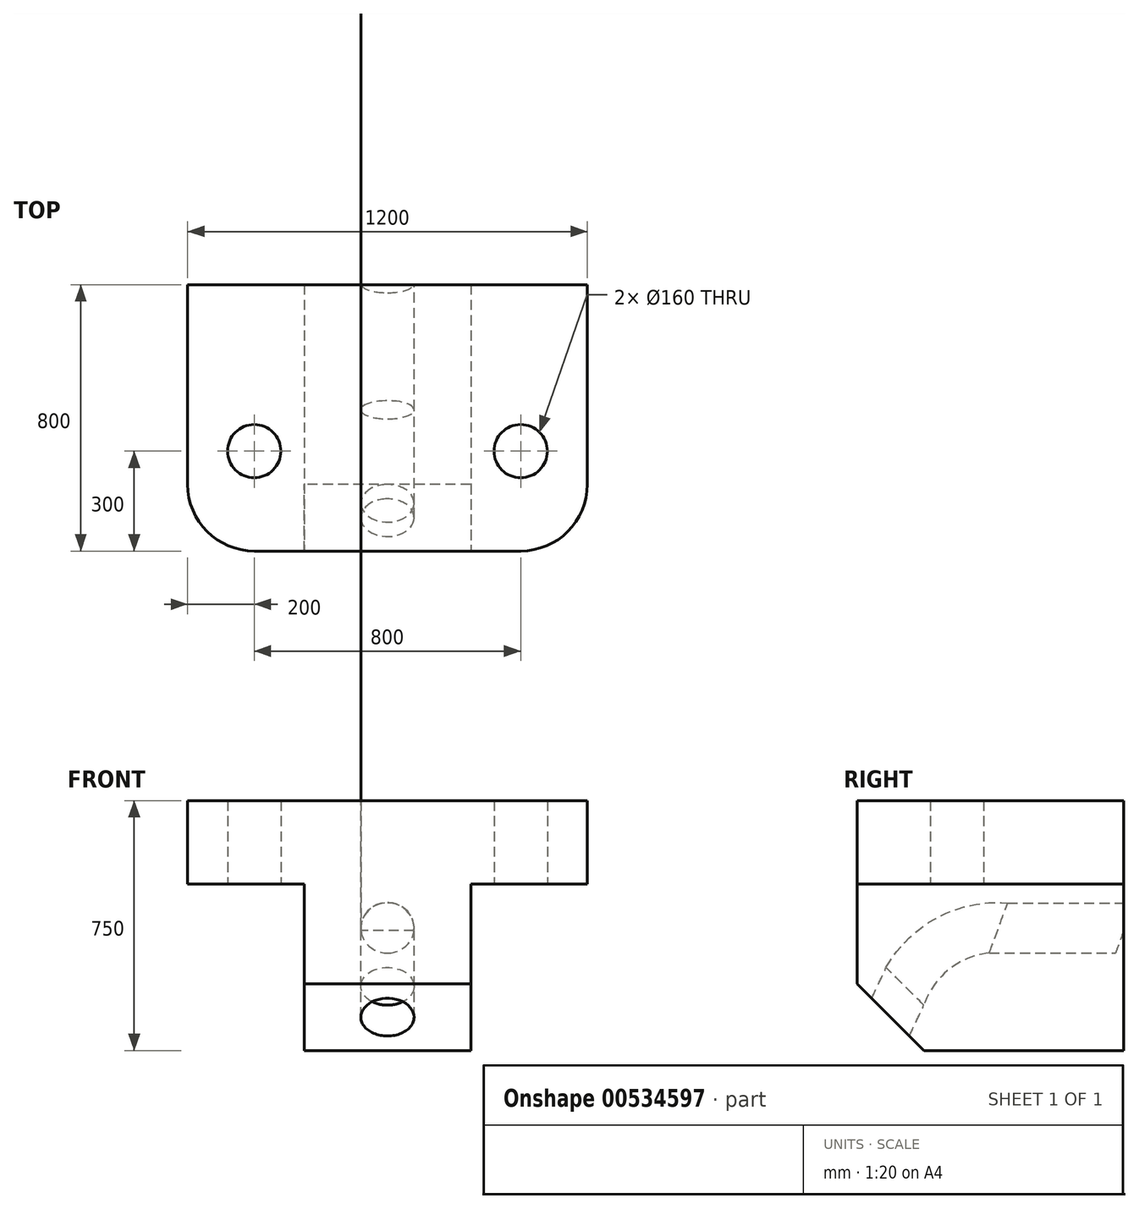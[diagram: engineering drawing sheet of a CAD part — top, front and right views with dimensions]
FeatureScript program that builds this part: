
annotation { "Feature Type Name" : "Feature", "Feature Type Description" : "" }
export const myFeature = defineFeature(function(context is Context, id is Id, definition is map)
    precondition{}
    {
        {
            var Q0;
            Q0=qCreatedBy(makeId("Top.planeOp"),FACE);
            var sketch = newSketch(context, id + "F0", { "sketchPlane" : qUnion([Q0])});
            skLineSegment(sketch, "E0.bottom", {"start": v(400, -400) * mm, "end": v(-400, -400) * mm});
            skLineSegment(sketch, "E0.top", {"start": v(600, 400) * mm, "end": v(-600, 400) * mm});
            skLineSegment(sketch, "E0.left", {"start": v(600, -200) * mm, "end": v(600, 400) * mm});
            skLineSegment(sketch, "E0.right", {"start": v(-600, -200) * mm, "end": v(-600, 400) * mm});
            skPoint(sketch, "E0.middle", {"position": v(0, 0) * mm});
            skPoint(sketch, "E1.visualSharp", {"position": v(-600, -400) * mm});
            skArc(sketch, "E1.filletArc", {"start": v(-600, -200) * mm, "mid": v(-541.42, -341.42) * mm, "end": v(-400, -400) * mm});
            skPoint(sketch, "E2.visualSharp", {"position": v(600, -400) * mm});
            skArc(sketch, "E2.filletArc", {"start": v(400, -400) * mm, "mid": v(541.42, -341.42) * mm, "end": v(600, -200) * mm});
            skSolve(sketch);
        }
        {
            var Q0;
            Q0 = qSketchRegion(id + "F0", true);
            extrude(context, id + "F1", {"entities" : qUnion([Q0]), "depth" : 250 * mm, "offsetDistance" : 25 * mm});
        }
        {
            var Q0;
            Q0=makeQuery(id+"F1.opExtrude","CAP_FACE",FACE,{"disambiguationData":[OSD([sQuery(id+"F0.wireOp",EDGE,"E0.bottom"),sQuery(id+"F0.wireOp",EDGE,"E0.top"),sQuery(id+"F0.wireOp",EDGE,"E0.left"),sQuery(id+"F0.wireOp",EDGE,"E0.right"),sQuery(id+"F0.wireOp",EDGE,"E1.filletArc"),sQuery(id+"F0.wireOp",EDGE,"E2.filletArc")])],"isStart":true});
            var sketch = newSketch(context, id + "F2", { "sketchPlane" : qUnion([Q0])});
            skCircle(sketch, "E3", {"center": v(-400, 100) * mm, "radius": 80 * mm});
            skCircle(sketch, "E4", {"center": v(400, 100) * mm, "radius": 80 * mm});
            skSolve(sketch);
        }
        {
            var Q0;
            Q0 = qSketchRegion(id + "F2", true);
            extrude(context, id + "F3", {"entities" : qUnion([Q0]), "operationType" : NewBodyOperationType.REMOVE, "oppositeDirection" : true, "depth" : 250 * mm, "offsetDistance" : 25 * mm});
        }
        {
            var Q0;
            Q0=makeQuery(id+"F1.opExtrude","CAP_FACE",FACE,{"disambiguationData":[OSD([sQuery(id+"F0.wireOp",EDGE,"E0.bottom"),sQuery(id+"F0.wireOp",EDGE,"E0.top"),sQuery(id+"F0.wireOp",EDGE,"E0.left"),sQuery(id+"F0.wireOp",EDGE,"E0.right"),sQuery(id+"F0.wireOp",EDGE,"E1.filletArc"),sQuery(id+"F0.wireOp",EDGE,"E2.filletArc")])],"isStart":true});
            var sketch = newSketch(context, id + "F4", { "sketchPlane" : qUnion([Q0])});
            skLineSegment(sketch, "E5.bottom", {"start": v(250, -400) * mm, "end": v(-250, -400) * mm});
            skLineSegment(sketch, "E5.top", {"start": v(250, 400) * mm, "end": v(-250, 400) * mm});
            skLineSegment(sketch, "E5.left", {"start": v(250, -400) * mm, "end": v(250, 400) * mm});
            skLineSegment(sketch, "E5.right", {"start": v(-250, -400) * mm, "end": v(-250, 400) * mm});
            skPoint(sketch, "E5.middle", {"position": v(0, 0) * mm});
            skSolve(sketch);
        }
        {
            var Q0;
            Q0 = qSketchRegion(id + "F4", true);
            extrude(context, id + "F5", {"entities" : qUnion([Q0]), "operationType" : NewBodyOperationType.ADD, "depth" : 500 * mm, "offsetDistance" : 25 * mm});
        }
        {
            var Q0;
            Q0=makeQuery(id+"F5.opExtrude","CAP_EDGE",EDGE,{"disambiguationData":[OSD([sQuery(id+"F4.wireOp",EDGE,"E5.top")])],"isStart":false});
            chamfer(context, id + "F6", {"entities" : qUnion([Q0]), "width" : 200 * mm, "tangentPropagation" : true});
        }
        {
            var Q0;
            Q0=makeQuery(id+"F6.opChamfer","BLEND_FACE",FACE,{"disambiguationData":[OSD([sQuery(id+"F4.wireOp",EDGE,"E5.top")])]});
            var sketch = newSketch(context, id + "F7", { "sketchPlane" : qUnion([Q0])});
            skCircle(sketch, "E6", {"center": v(0, -70.69) * mm, "radius": 80 * mm});
            skSolve(sketch);
        }
        {
            var Q0;
            Q0=makeQuery(id+"F5.opExtrude","SWEPT_FACE",FACE,{"disambiguationData":[OSD([sQuery(id+"F4.wireOp",EDGE,"E5.right")])]});
            var sketch = newSketch(context, id + "F8", { "sketchPlane" : qUnion([Q0])});
            skLineSegment(sketch, "E7", {"start": v(-21.12, -140) * mm, "end": v(-400, -140) * mm});
            skLineSegment(sketch, "E8", {"start": v(310.89, -442.19) * mm, "end": v(250.8, -313.26) * mm});
            skPoint(sketch, "E9.visualSharp", {"position": v(170.04, -140) * mm});
            skArc(sketch, "E9.filletArc", {"start": v(250.8, -313.26) * mm, "mid": v(140.1, -187) * mm, "end": v(-21.12, -140) * mm});
            skSolve(sketch);
        }
        {
            var Q0;
            Q0=makeQuery(id+"F7.imprint","IMPRINT",FACE,{"disambiguationData":[TD([[makeQuery(id+"F7.imprint","IMPRINT",EDGE,{"derivedFrom":sQuery(id+"F7.wireOp",EDGE,"E6")}),1.0]])]});
            var Q1;
            Q1=sQuery(id+"F8.wireOp",EDGE,"E8");
            var Q2;
            Q2=sQuery(id+"F8.wireOp",EDGE,"E9.filletArc");
            var Q3;
            Q3=sQuery(id+"F8.wireOp",EDGE,"E7");
            sweep(context, id + "F9", {"operationType" : NewBodyOperationType.REMOVE, "profiles" : qUnion([Q0]), "path" : qUnion([Q1, Q2, Q3])});
        }
    });
